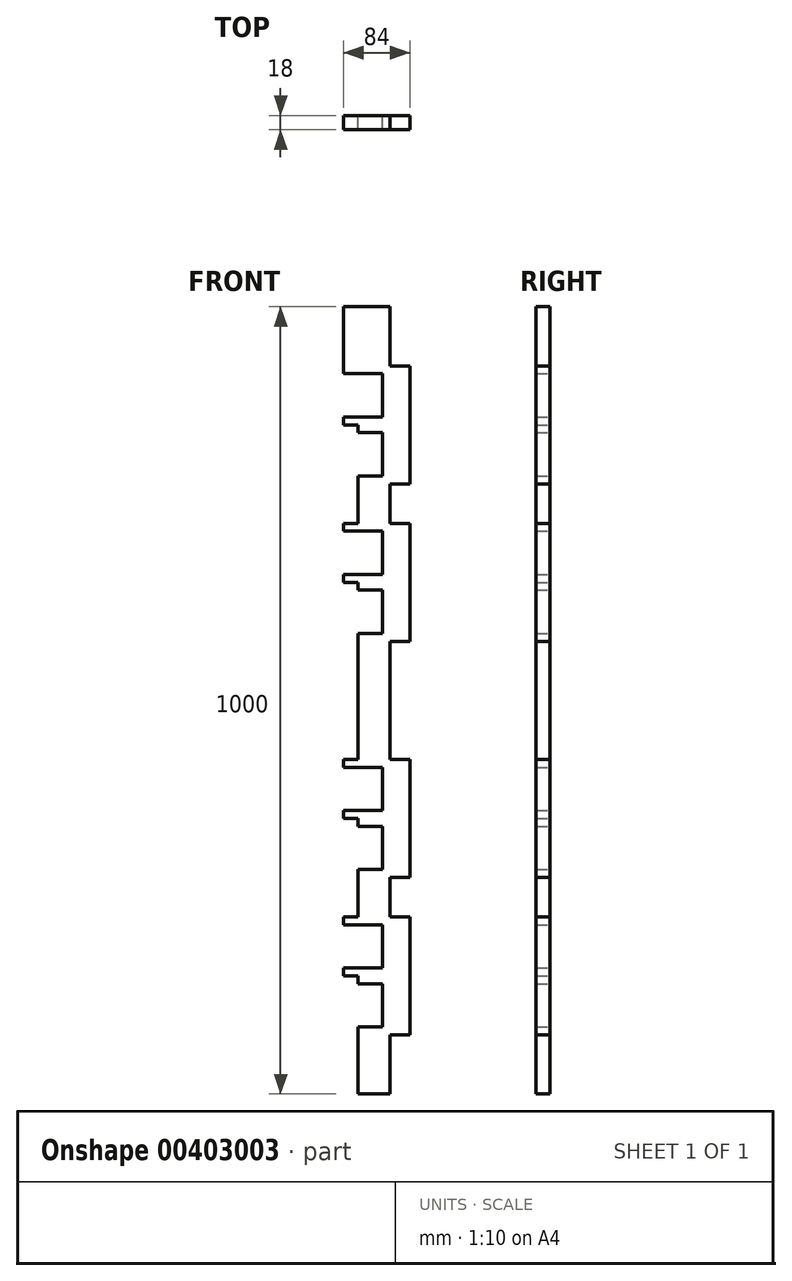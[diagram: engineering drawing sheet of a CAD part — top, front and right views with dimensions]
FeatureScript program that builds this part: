
annotation { "Feature Type Name" : "Feature", "Feature Type Description" : "" }
export const myFeature = defineFeature(function(context is Context, id is Id, definition is map)
    precondition{}
    {
        {
            var Q0;
            Q0=qCreatedBy(makeId("Front.planeOp"),FACE);
            var sketch = newSketch(context, id + "F0", { "sketchPlane" : qUnion([Q0])});
            skLineSegment(sketch, "E0.right", {"start": v(41, 0) * mm, "end": v(41, 75) * mm});
            skLineSegment(sketch, "E1.bottom", {"start": v(41, 925) * mm, "end": v(66, 925) * mm});
            skLineSegment(sketch, "E1.top", {"start": v(41, 775) * mm, "end": v(66, 775) * mm});
            skLineSegment(sketch, "E1.right", {"start": v(66, 925) * mm, "end": v(66, 775) * mm});
            skLineSegment(sketch, "E2.bottom", {"start": v(41, 425) * mm, "end": v(66, 425) * mm});
            skLineSegment(sketch, "E2.top", {"start": v(41, 275) * mm, "end": v(66, 275) * mm});
            skLineSegment(sketch, "E2.right", {"start": v(66, 425) * mm, "end": v(66, 275) * mm});
            skLineSegment(sketch, "E3.trimOffspring", {"start": v(41, 925) * mm, "end": v(41, 1000) * mm});
            skLineSegment(sketch, "E4.trimOffspring", {"start": v(41, 425) * mm, "end": v(41, 575) * mm});
            skLineSegment(sketch, "E5.bottom", {"start": v(66, 725) * mm, "end": v(41, 725) * mm});
            skLineSegment(sketch, "E5.top", {"start": v(66, 575) * mm, "end": v(41, 575) * mm});
            skLineSegment(sketch, "E5.right", {"start": v(66, 725) * mm, "end": v(66, 575) * mm});
            skLineSegment(sketch, "E6.bottom", {"start": v(66, 225) * mm, "end": v(41, 225) * mm});
            skLineSegment(sketch, "E6.top", {"start": v(66, 75) * mm, "end": v(41, 75) * mm});
            skLineSegment(sketch, "E6.right", {"start": v(66, 225) * mm, "end": v(66, 75) * mm});
            skLineSegment(sketch, "E7.trimOffspring", {"start": v(41, 725) * mm, "end": v(41, 775) * mm});
            skLineSegment(sketch, "E8.trimOffspring", {"start": v(41, 225) * mm, "end": v(41, 275) * mm});
            skPoint(sketch, "E9.orphan", {"position": v(0, 0) * mm});
            skLineSegment(sketch, "E10.right", {"start": v(-18, 1000) * mm, "end": v(-18, 915) * mm});
            skLineSegment(sketch, "E11.bottom", {"start": v(-18, 725) * mm, "end": v(0, 725) * mm});
            skLineSegment(sketch, "E11.right", {"start": v(-18, 725) * mm, "end": v(-18, 715) * mm});
            skLineSegment(sketch, "E12.bottom", {"start": v(-18, 425) * mm, "end": v(0, 425) * mm});
            skLineSegment(sketch, "E12.right", {"start": v(-18, 425) * mm, "end": v(-18, 415) * mm});
            skLineSegment(sketch, "E13.bottom", {"start": v(-18, 225) * mm, "end": v(0, 225) * mm});
            skLineSegment(sketch, "E14.bottom", {"start": v(-18, 850) * mm, "end": v(0, 850) * mm});
            skLineSegment(sketch, "E14.top", {"start": v(-18, 650) * mm, "end": v(0, 650) * mm});
            skLineSegment(sketch, "E15.bottom", {"start": v(-18, 350) * mm, "end": v(0, 350) * mm});
            skLineSegment(sketch, "E15.top", {"start": v(-18, 150) * mm, "end": v(0, 150) * mm});
            skLineSegment(sketch, "E16", {"start": v(0, 850) * mm, "end": v(0, 840) * mm});
            skLineSegment(sketch, "E17", {"start": v(0, 650) * mm, "end": v(0, 640) * mm});
            skLineSegment(sketch, "E18", {"start": v(0, 350) * mm, "end": v(0, 340) * mm});
            skLineSegment(sketch, "E19", {"start": v(0, 150) * mm, "end": v(0, 140) * mm});
            skLineSegment(sketch, "E20", {"start": v(-18, 1000) * mm, "end": v(41, 1000) * mm});
            skLineSegment(sketch, "E21", {"start": v(0, 0) * mm, "end": v(41, 0) * mm});
            skLineSegment(sketch, "E22", {"start": v(-18, 150) * mm, "end": v(-18, 160) * mm});
            skLineSegment(sketch, "E23.bottom", {"start": v(-18, 915) * mm, "end": v(31, 915) * mm});
            skLineSegment(sketch, "E23.top", {"start": v(-18, 860) * mm, "end": v(31, 860) * mm});
            skLineSegment(sketch, "E23.right", {"start": v(31, 915) * mm, "end": v(31, 860) * mm});
            skLineSegment(sketch, "E24.bottom", {"start": v(-18, 715) * mm, "end": v(31, 715) * mm});
            skLineSegment(sketch, "E24.top", {"start": v(-18, 660) * mm, "end": v(31, 660) * mm});
            skLineSegment(sketch, "E24.right", {"start": v(31, 715) * mm, "end": v(31, 660) * mm});
            skLineSegment(sketch, "E25.bottom", {"start": v(-18, 415) * mm, "end": v(31, 415) * mm});
            skLineSegment(sketch, "E25.top", {"start": v(-18, 360) * mm, "end": v(31, 360) * mm});
            skLineSegment(sketch, "E25.right", {"start": v(31, 415) * mm, "end": v(31, 360) * mm});
            skLineSegment(sketch, "E26.bottom", {"start": v(-18, 215) * mm, "end": v(31, 215) * mm});
            skLineSegment(sketch, "E26.top", {"start": v(-18, 160) * mm, "end": v(31, 160) * mm});
            skLineSegment(sketch, "E26.right", {"start": v(31, 215) * mm, "end": v(31, 160) * mm});
            skLineSegment(sketch, "E27.trimOffspring", {"start": v(-18, 860) * mm, "end": v(-18, 850) * mm});
            skLineSegment(sketch, "E28.trimOffspring", {"start": v(-18, 660) * mm, "end": v(-18, 650) * mm});
            skLineSegment(sketch, "E29.trimOffspring", {"start": v(-18, 360) * mm, "end": v(-18, 350) * mm});
            skLineSegment(sketch, "E30.trimOffspring", {"start": v(-18, 215) * mm, "end": v(-18, 225) * mm});
            skLineSegment(sketch, "E31.bottom", {"start": v(0, 840) * mm, "end": v(31, 840) * mm});
            skLineSegment(sketch, "E31.top", {"start": v(0, 785) * mm, "end": v(31, 785) * mm});
            skLineSegment(sketch, "E31.right", {"start": v(31, 840) * mm, "end": v(31, 785) * mm});
            skLineSegment(sketch, "E32.bottom", {"start": v(0, 640) * mm, "end": v(31, 640) * mm});
            skLineSegment(sketch, "E32.top", {"start": v(0, 585) * mm, "end": v(31, 585) * mm});
            skLineSegment(sketch, "E32.right", {"start": v(31, 640) * mm, "end": v(31, 585) * mm});
            skLineSegment(sketch, "E33.bottom", {"start": v(0, 340) * mm, "end": v(31, 340) * mm});
            skLineSegment(sketch, "E33.top", {"start": v(0, 285) * mm, "end": v(31, 285) * mm});
            skLineSegment(sketch, "E33.right", {"start": v(31, 340) * mm, "end": v(31, 285) * mm});
            skLineSegment(sketch, "E34.bottom", {"start": v(0, 140) * mm, "end": v(31, 140) * mm});
            skLineSegment(sketch, "E34.top", {"start": v(0, 85) * mm, "end": v(31, 85) * mm});
            skLineSegment(sketch, "E34.right", {"start": v(31, 140) * mm, "end": v(31, 85) * mm});
            skLineSegment(sketch, "E35.trimOffspring", {"start": v(0, 785) * mm, "end": v(0, 725) * mm});
            skLineSegment(sketch, "E36.trimOffspring", {"start": v(0, 585) * mm, "end": v(0, 425) * mm});
            skLineSegment(sketch, "E37.trimOffspring", {"start": v(0, 285) * mm, "end": v(0, 225) * mm});
            skLineSegment(sketch, "E38.trimOffspring", {"start": v(0, 85) * mm, "end": v(0, 0) * mm});
            skSolve(sketch);
        }
        {
            var Q0;
            Q0=makeQuery(id+"F0.imprint","IMPRINT",FACE,{"disambiguationData":[TD([[makeQuery(id+"F0.imprint","IMPRINT",EDGE,{"derivedFrom":sQuery(id+"F0.wireOp",EDGE,"E0.right")}),1.0]])]});
            extrude(context, id + "F1", {"entities" : qUnion([Q0]), "depth" : 18 * mm});
        }
    });
